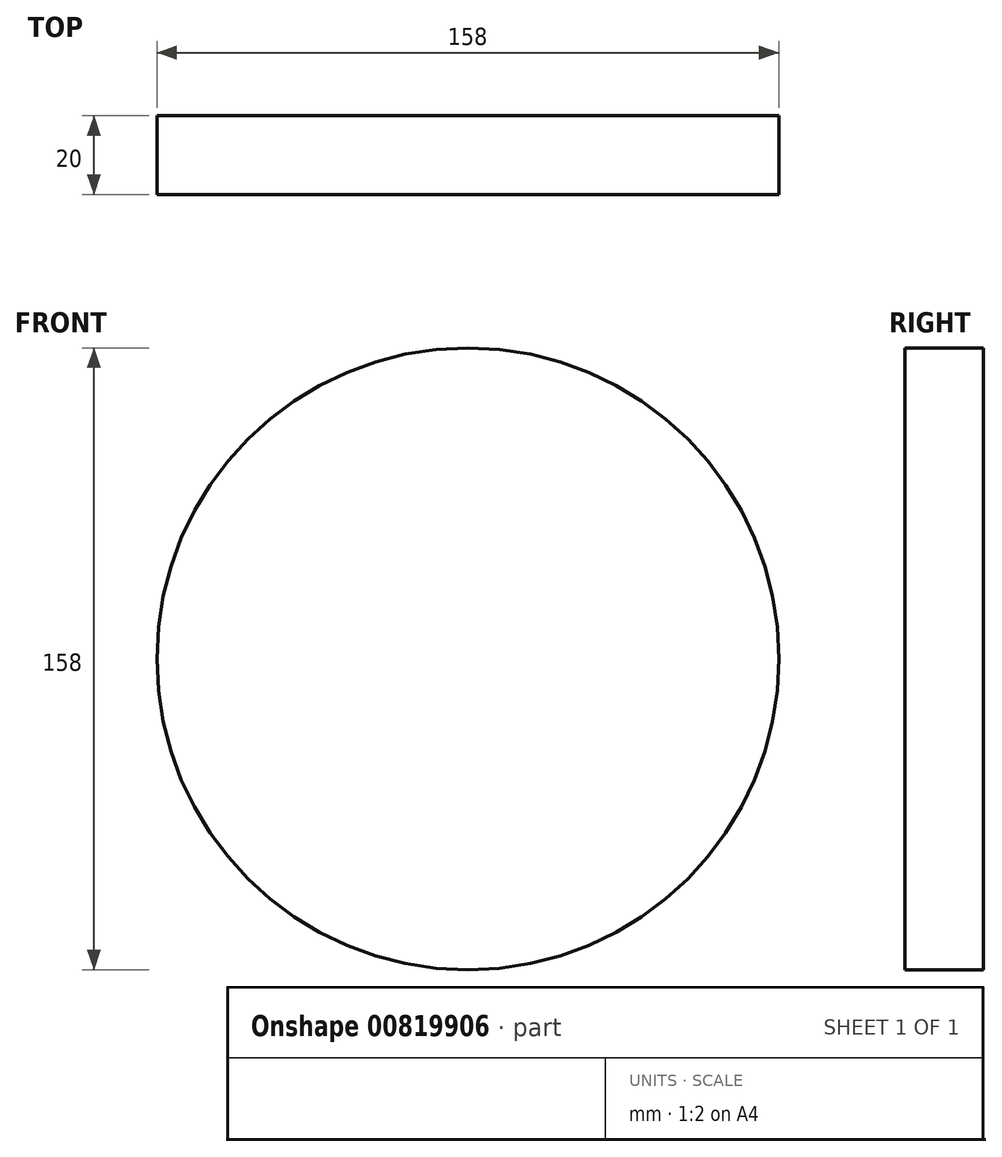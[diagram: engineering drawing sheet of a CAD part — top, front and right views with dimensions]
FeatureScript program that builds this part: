
annotation { "Feature Type Name" : "Feature", "Feature Type Description" : "" }
export const myFeature = defineFeature(function(context is Context, id is Id, definition is map)
    precondition{}
    {
        {
            var Q0;
            Q0=qCreatedBy(makeId("Front.planeOp"),FACE);
            var sketch = newSketch(context, id + "F0", { "sketchPlane" : qUnion([Q0])});
            skCircle(sketch, "E0", {"center": v(-0.48, 1.12) * mm, "radius": 79 * mm});
            skSolve(sketch);
        }
        {
            var Q0;
            Q0=qSketchRegion(id+"F0",true);
            var Q1;
            Q1=makeQuery(id+"F0.imprint","IMPRINT",FACE,{"disambiguationData":[TD([[makeQuery(id+"F0.imprint","IMPRINT",EDGE,{"derivedFrom":sQuery(id+"F0.wireOp",EDGE,"E0")}),1.0]])]});
            extrude(context, id + "F1", {"entities" : qUnion([Q0, Q1]), "depth" : 20 * mm, "offsetDistance" : 25 * mm});
        }
    });
